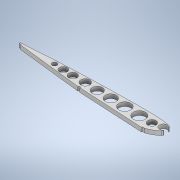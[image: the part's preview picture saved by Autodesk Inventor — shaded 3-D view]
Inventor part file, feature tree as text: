
AUTODESK INVENTOR PART (.ipt)
format: ipt  version: 2022 (Build 260153000, 153)  size: 278,528 bytes
history: native  units: mm
features: extrude x1, sketch x1
ambient origin geometry x8: Origin, YZ Plane, XZ Plane, XY Plane, X Axis, Y Axis, Z Axis, Center Point
bodies: Body1 (feature_tree)
feature tree (2):
  extrude  "Extrusion5"  Depth=10.0mm
  sketch  "Sketch1"  dims[d31=34.456mm d50=368.759386mm d57=16.0mm d69=8.0mm d70=20.0mm d80=19.0mm d81=16.0mm d82=1.0mm d83=1.0mm d84=1.0mm d85=1.0mm d86=1.0mm d87=0.8mm d88=1.0mm d90=19.0mm d94=5.0mm d95=5.0mm d101=5.0mm d102=5.0mm d105=5.0mm d106=5.0mm d108=2.0mm d109=22.0mm d110=30.0mm d111=29.0mm d112=27.0mm d113=25.0mm d114=10.0mm d115=0.0mm]
